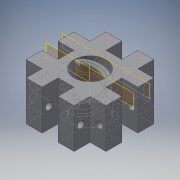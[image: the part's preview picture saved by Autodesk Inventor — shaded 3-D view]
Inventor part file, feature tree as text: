
AUTODESK INVENTOR PART (.ipt)
format: ipt  version: 2017 (Build 210142000, 142)  size: 327,680 bytes
history: native  units: mm
features: sketch x4, extrude x3, plane x2, pattern_circular x1, other x1, helix x1, fillet x1
ambient origin geometry x8: Origin, YZ Plane, XZ Plane, XY Plane, X Axis, Y Axis, Z Axis, Center Point
bodies: Solid1 (feature_tree)
feature tree (13):
  extrude  "Extrusion1"  Depth=13.0mm
  extrude  "Extrusion6"  Depth=7.0mm
  extrude  "Extrusion7"  Depth=7.0mm
  pattern_circular  "Circular Pattern3"  [2 undecoded]
  plane  "Work Plane3"
  sketch  "Sketch10"  dims[d59=7.0mm d60=7.0mm d61=7.0mm d62=90.0deg d63=7.0mm d64=7.0mm d65=90.0deg d66=7.0mm d67=7.0mm d68=7.0mm d69=7.0mm d70=7.0mm d71=7.0mm d72=7.0mm d73=7.0mm d74=7.0mm d75=7.0mm d76=7.0mm d77=90.0deg d78=13.0mm d81=10.0mm d82=0.0mm d83=3.0mm d84=3.0mm d85=10.0mm d86=0.0mm d87=40.0mm d88=360.0deg d93=7.0mm d94=14.0mm d95=7.0mm d100=2.5mm d101=5.0mm d102=12.5mm d103=10.0mm d104=10.0mm d105=0.0mm d106=90.0deg d107=90.0deg d108=0.0mm d109=0.0mm d110=1.0mm]
  other  "Work Axis1"
  helix  "Coil1"  [1 undecoded]
  fillet  "Fillet3"  [1 undecoded]
  sketch  "Sketch1"  dims[d28=17.5mm d29=0.0mm d49=13.0mm]
  sketch  "Sketch6"  dims[d55=7.0mm d56=7.0mm]
  sketch  "Sketch7"  dims[d57=7.0mm d58=7.0mm]
  plane  "Work Plane2"
note: 4 required parameter values undecoded (feature->parameter linkage not recoverable at this tier; creation-order binding heuristic only, values carry confidence <= 0.55)
